# Revit family: GALAD Вектор LED
name_source: partatom
category: Осветительные приборы
revit_build: Autodesk Revit 2018 (Build: 20180423_1000(x64)
units: mm (PartAtom-declared; Revit-internal decimal feet)

## family parameters
Источник света = Да
Общий = Нет
Основа = Грань
При загрузке вырезать с полостями = Нет
Размер круглого соединителя = Использовать диаметр
Тип детали = Нормальный
Точка расчета площади = Нет

## types (1)
- GALAD Вектор LED
    ADSK_Версия Revit = 2018
    ADSK_Версия семейства = 1.01
    ADSK_Единица измерения = шт.
    ADSK_Завод-изготовитель = АО «КАДОШКИНСКИЙ ЭЛЕКТРОТЕХНИЧЕСКИЙ ЗАВОД»
    ADSK_Классификация нагрузок = Освещение
    ADSK_Код изделия = 11018
    ADSK_Количество = 1
    ADSK_Количество фаз = 1
    ADSK_Коэффициент мощности = 0.96
    ADSK_Марка = GALAD Вектор LED-20-4000
    ADSK_Масса = 6.7
    ADSK_Масса_Текст = 6.7
    ADSK_Наименование = GALAD Вектор LED-20-4000
    ADSK_Наименование краткое = GALAD Вектор LED-20-4000
    ADSK_Напряжение = 230 В
    ADSK_Номинальная мощность = 20 В·А
    ADSK_Обозначение = ГОСТ 15150-69
    ADSK_Полная мощность = 21 В·А
    ADSK_Размер_Высота = 0 мм
    ADSK_Размер_Длина = 1200 мм
    ADSK_Размер_Ширина = 0 мм
    ADSK_Ток = 0 А
    ADSK_Энергоэффективность = 85 лм/Вт
    IP = 20
    URL = https://galad.ru
    Видимая форма излучения при визуализации = Нет
    Возможный угол наклона = 0
    Группа модели = Светильники
    Диапазон цветовой температуры = 3985±275
    Изготовитель = АО «КАДОШКИНСКИЙ ЭЛЕКТРОТЕХНИЧЕСКИЙ ЗАВОД»
    Излучение по длине прямоугольника = 102 мм
    Излучение по ширине прямоугольника = 1170 мм
    Класс Защиты = 1
    Класс защиты от поражения электрическим током = 1
    Класс светораспределения = П
    Климатическая зона = УХЛ4
    Климатическое исполнение = 1…35 °С
    Коэффициент пульсации = менее 5%
    Материал корпуса = Сталь
    Материал рассеивателя = Стекло
    Неравномерность яркости = 0
    Область использования = образовательные учреждения
    Описание = GALAD Вектор LED - это светодиодный светильник для освещения школьных досок, устанавливается на специальных кронштейнах над доской. Специальное светораспределение светильника создает равномерное заливающее освещение доски комфортное для работы и глаз учащихся. Высокая цветопередача, низкие пульсации, стабильная во времени цветовая температура и качественные комплектующие.
    Отметка по умолчанию = 1219 мм
    Полная установленная мощность = 21 В·А
    Световая отдача = 85
    Светофильтр = 16777215
    Смещение цветовой температуры при затухании лампы = <Нет>
    Снижение светового потока во время разгорания = не более 6%
    Срок службы = 12 лет
    Тип КСС = специальная
    Тип ПРА = ЭПРА
    Тип источника света = LED
    Тип монтажной поверхности = Настенный
    Тип продукции = Светильник
    Тип устройства управления светодиодами = без управления
    Угол наклона = 60.00°
    Файл фотометрической сетки = Cvetilnik GALAD vektor LED-20-4000.IES
    Цветопередача = 80
    Частота = 50
